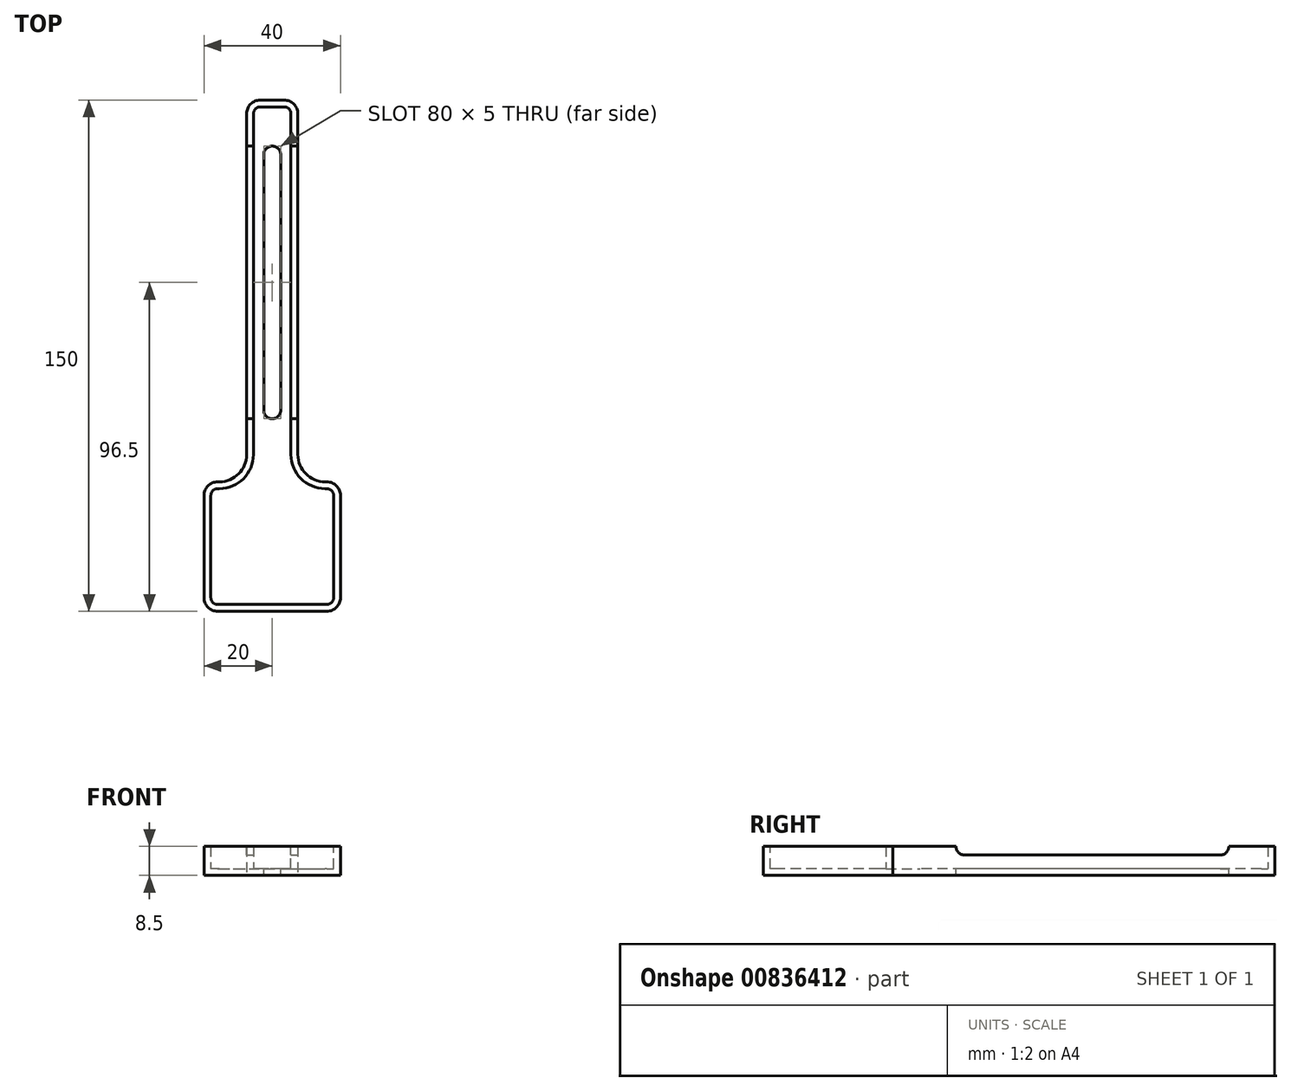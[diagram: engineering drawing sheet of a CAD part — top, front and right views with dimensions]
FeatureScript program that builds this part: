
annotation { "Feature Type Name" : "Feature", "Feature Type Description" : "" }
export const myFeature = defineFeature(function(context is Context, id is Id, definition is map)
    precondition{}
    {
        {
            assignVariable(context, id + "F0", {"name" : "WallThickness", "anyValue" : 2});
        }
        {
            assignVariable(context, id + "F1", {"name" : "SensorWidth", "anyValue" : 11});
        }
        {
            var Q0;
            Q0=qCreatedBy(makeId("Top.planeOp"),FACE);
            var sketch = newSketch(context, id + "F2", { "sketchPlane" : qUnion([Q0])});
            skLineSegment(sketch, "E0", {"start": v(-20, 19) * mm, "end": v(-20, -19) * mm});
            skLineSegment(sketch, "E1", {"start": v(-20, -19) * mm, "end": v(20, -19) * mm});
            skLineSegment(sketch, "E2", {"start": v(20, -19) * mm, "end": v(20, 19) * mm});
            skLineSegment(sketch, "E3", {"start": v(20, 19) * mm, "end": v(7.5, 19) * mm});
            skLineSegment(sketch, "E4", {"start": v(7.5, 19) * mm, "end": v(7.5, 131) * mm});
            skLineSegment(sketch, "E5", {"start": v(7.5, 131) * mm, "end": v(-7.5, 131) * mm});
            skLineSegment(sketch, "E6", {"start": v(-7.5, 131) * mm, "end": v(-7.5, 19) * mm});
            skLineSegment(sketch, "E7", {"start": v(-7.5, 19) * mm, "end": v(-20, 19) * mm});
            skLineSegment(sketch, "E8", {"start": v(-7.5, 19) * mm, "end": v(7.5, 19) * mm, "construction": true});
            skSolve(sketch);
        }
        {
            var Q0;
            Q0 = qSketchRegion(id + "F2", true);
            extrude(context, id + "F3", {"entities" : qUnion([Q0]), "depth" : ((getVariable(context, 'SensorWidth') * 0.5) + getVariable(context, 'WallThickness') + 1) * mm, "offsetDistance" : 25 * mm});
        }
        {
            var Q0;
            Q0=makeQuery(id+"F3.opExtrude","SWEPT_EDGE",EDGE,{"disambiguationData":[OSD([sQuery(id+"F2.wireOp",EDGE,"E0"),sQuery(id+"F2.wireOp",EDGE,"E7")])]});
            var Q1;
            Q1=makeQuery(id+"F3.opExtrude","SWEPT_EDGE",EDGE,{"disambiguationData":[OSD([sQuery(id+"F2.wireOp",EDGE,"E0"),sQuery(id+"F2.wireOp",EDGE,"E1")])]});
            var Q2;
            Q2=makeQuery(id+"F3.opExtrude","SWEPT_EDGE",EDGE,{"disambiguationData":[OSD([sQuery(id+"F2.wireOp",EDGE,"E1"),sQuery(id+"F2.wireOp",EDGE,"E2")])]});
            var Q3;
            Q3=makeQuery(id+"F3.opExtrude","SWEPT_EDGE",EDGE,{"disambiguationData":[OSD([sQuery(id+"F2.wireOp",EDGE,"E2"),sQuery(id+"F2.wireOp",EDGE,"E3")])]});
            var Q4;
            Q4=makeQuery(id+"F3.opExtrude","SWEPT_EDGE",EDGE,{"disambiguationData":[OSD([sQuery(id+"F2.wireOp",EDGE,"E4"),sQuery(id+"F2.wireOp",EDGE,"E5")])]});
            var Q5;
            Q5=makeQuery(id+"F3.opExtrude","SWEPT_EDGE",EDGE,{"disambiguationData":[OSD([sQuery(id+"F2.wireOp",EDGE,"E5"),sQuery(id+"F2.wireOp",EDGE,"E6")])]});
            fillet(context, id + "F4", {"entities" : qUnion([Q0, Q1, Q2, Q3, Q4, Q5]), "radius" : 4 * mm, "tangentPropagation" : true, "allowEdgeOverflow" : false});
        }
        {
            var Q0;
            Q0=makeQuery(id+"F3.opExtrude","SWEPT_EDGE",EDGE,{"disambiguationData":[OSD([sQuery(id+"F2.wireOp",EDGE,"E3"),sQuery(id+"F2.wireOp",EDGE,"E4")])]});
            var Q1;
            Q1=makeQuery(id+"F3.opExtrude","SWEPT_EDGE",EDGE,{"disambiguationData":[OSD([sQuery(id+"F2.wireOp",EDGE,"E6"),sQuery(id+"F2.wireOp",EDGE,"E7")])]});
            fillet(context, id + "F5", {"entities" : qUnion([Q0, Q1]), "radius" : 8 * mm, "tangentPropagation" : true, "allowEdgeOverflow" : false});
        }
        {
            var Q0;
            Q0=makeQuery(id+"F3.opExtrude","CAP_FACE",FACE,{"disambiguationData":[OSD([sQuery(id+"F2.wireOp",EDGE,"E0"),sQuery(id+"F2.wireOp",EDGE,"E1"),sQuery(id+"F2.wireOp",EDGE,"E2"),sQuery(id+"F2.wireOp",EDGE,"E3"),sQuery(id+"F2.wireOp",EDGE,"E4"),sQuery(id+"F2.wireOp",EDGE,"E5"),sQuery(id+"F2.wireOp",EDGE,"E6"),sQuery(id+"F2.wireOp",EDGE,"E7")])],"isStart":false});
            shell(context, id + "F6", {"entities" : qUnion([Q0]), "thickness" : (getVariable(context, 'WallThickness')) * mm});
        }
        {
            var Q0;
            Q0=makeQuery(id+"F6.opShell","OFFSET_FACE",FACE,{"disambiguationData":[OSD([sQuery(id+"F2.wireOp",EDGE,"E0"),sQuery(id+"F2.wireOp",EDGE,"E1"),sQuery(id+"F2.wireOp",EDGE,"E2"),sQuery(id+"F2.wireOp",EDGE,"E3"),sQuery(id+"F2.wireOp",EDGE,"E4"),sQuery(id+"F2.wireOp",EDGE,"E5"),sQuery(id+"F2.wireOp",EDGE,"E6"),sQuery(id+"F2.wireOp",EDGE,"E7")])]});
            var sketch = newSketch(context, id + "F7", { "sketchPlane" : qUnion([Q0])});
            skLineSegment(sketch, "E9.left", {"start": v(-2.5, 115) * mm, "end": v(-2.5, 40) * mm});
            skLineSegment(sketch, "E9.right", {"start": v(2.5, 115) * mm, "end": v(2.5, 40) * mm});
            skArc(sketch, "E10", {"start": v(-2.5, 115) * mm, "mid": v(0, 117.5) * mm, "end": v(2.5, 115) * mm});
            skArc(sketch, "E11", {"start": v(2.5, 40) * mm, "mid": v(0, 37.5) * mm, "end": v(-2.5, 40) * mm});
            skSolve(sketch);
        }
        {
            var Q0;
            Q0 = qSketchRegion(id + "F7", true);
            extrude(context, id + "F8", {"entities" : qUnion([Q0]), "operationType" : NewBodyOperationType.REMOVE, "endBound" : BoundingType.UP_TO_NEXT, "oppositeDirection" : true, "depth" : 25 * mm, "offsetDistance" : 25 * mm});
        }
        {
            var Q0;
            Q0=makeQuery(id+"F3.opExtrude","SWEPT_FACE",FACE,{"disambiguationData":[OSD([sQuery(id+"F2.wireOp",EDGE,"E4")])]});
            var sketch = newSketch(context, id + "F9", { "sketchPlane" : qUnion([Q0])});
            skLineSegment(sketch, "E12.bottom", {"start": v(40, 11) * mm, "end": v(115, 11) * mm});
            skLineSegment(sketch, "E12.top", {"start": v(40, 6) * mm, "end": v(115, 6) * mm});
            skArc(sketch, "E13", {"start": v(40, 11) * mm, "mid": v(37.5, 8.5) * mm, "end": v(40, 6) * mm});
            skArc(sketch, "E14", {"start": v(115, 11) * mm, "mid": v(117.5, 8.5) * mm, "end": v(115, 6) * mm});
            skLineSegment(sketch, "E15", {"start": v(40, 11) * mm, "end": v(40, 6) * mm, "construction": true});
            skLineSegment(sketch, "E16", {"start": v(115, 11) * mm, "end": v(115, 6) * mm, "construction": true});
            skSolve(sketch);
        }
        {
            var Q0;
            Q0 = qSketchRegion(id + "F9", true);
            extrude(context, id + "F10", {"entities" : qUnion([Q0]), "operationType" : NewBodyOperationType.REMOVE, "oppositeDirection" : true, "depth" : (getVariable(context, 'SensorWidth') + (2 * getVariable(context, 'WallThickness'))) * mm, "offsetDistance" : 25 * mm});
        }
    });
